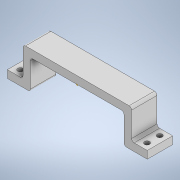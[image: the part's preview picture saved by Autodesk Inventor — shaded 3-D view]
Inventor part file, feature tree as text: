
AUTODESK INVENTOR PART (.ipt)
format: ipt  version: 2022 (Build 260153000, 153)  size: 141,824 bytes
history: native  units: mm
features: extrude x2, sketch x2, mirror x1, other x1
ambient origin geometry x8: Origin, YZ Plane, XZ Plane, XY Plane, X Axis, Y Axis, Z Axis, Center Point
bodies: Solid1 (feature_tree)
feature tree (6):
  extrude  "Extrusion1"  Depth=6.0mm
  extrude  "Extrusion2"  Depth=2.0mm
  mirror  "Mirror1"
  other  "Work Point1"
  sketch  "Sketch1"  dims[d0=6.0mm d1=6.0mm]
  sketch  "Sketch2"  dims[d2=6.0mm d3=2.0mm d4=20.0mm d5=0.0mm d7=10.0mm d8=5.0mm d9=4.0mm d10=4.0mm d11=20.0mm d12=0.0mm]
